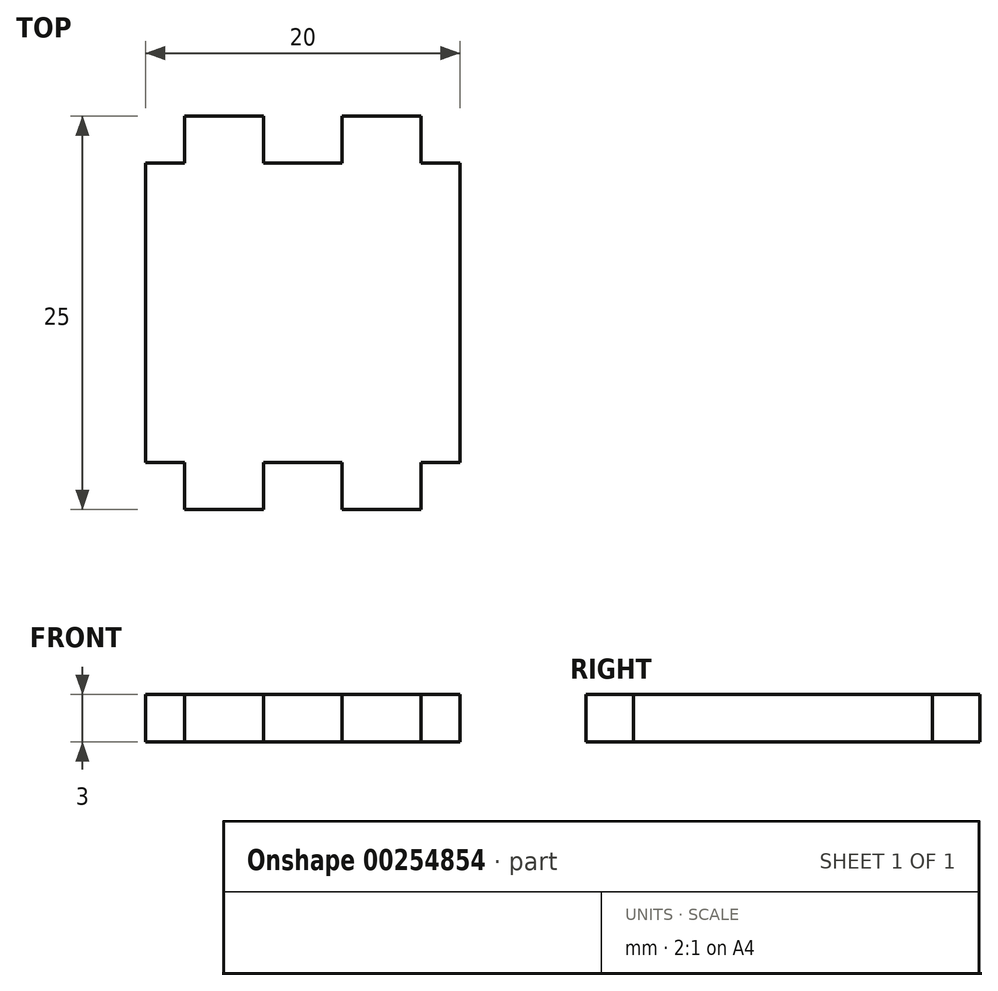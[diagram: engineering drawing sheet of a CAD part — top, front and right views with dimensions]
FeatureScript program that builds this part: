
annotation { "Feature Type Name" : "Feature", "Feature Type Description" : "" }
export const myFeature = defineFeature(function(context is Context, id is Id, definition is map)
    precondition{}
    {
        {
            var Q0;
            Q0=qCreatedBy(makeId("Top.planeOp"),FACE);
            var sketch = newSketch(context, id + "F0", { "sketchPlane" : qUnion([Q0])});
            skLineSegment(sketch, "E0", {"start": v(-10, 0) * mm, "end": v(-10, 9.5) * mm});
            skLineSegment(sketch, "E1", {"start": v(-10, 9.5) * mm, "end": v(-7.5, 9.5) * mm});
            skLineSegment(sketch, "E2", {"start": v(-7.5, 9.5) * mm, "end": v(-7.5, 12.5) * mm});
            skLineSegment(sketch, "E3", {"start": v(-7.5, 12.5) * mm, "end": v(-2.5, 12.5) * mm});
            skLineSegment(sketch, "E4", {"start": v(-2.5, 12.5) * mm, "end": v(-2.5, 9.5) * mm});
            skLineSegment(sketch, "E5", {"start": v(-2.5, 9.5) * mm, "end": v(0, 9.5) * mm});
            skLineSegment(sketch, "E6.MirrorCS", {"start": v(2.5, 9.5) * mm, "end": v(0, 9.5) * mm});
            skLineSegment(sketch, "E7.MirrorCS", {"start": v(2.5, 12.5) * mm, "end": v(2.5, 9.5) * mm});
            skLineSegment(sketch, "E8.MirrorCS", {"start": v(7.5, 12.5) * mm, "end": v(2.5, 12.5) * mm});
            skLineSegment(sketch, "E9.MirrorCS", {"start": v(7.5, 9.5) * mm, "end": v(7.5, 12.5) * mm});
            skLineSegment(sketch, "E10.MirrorCS", {"start": v(10, 9.5) * mm, "end": v(7.5, 9.5) * mm});
            skLineSegment(sketch, "E11.MirrorCS", {"start": v(10, 0) * mm, "end": v(10, 9.5) * mm});
            skLineSegment(sketch, "E12.MirrorCS", {"start": v(10, 0) * mm, "end": v(10, -9.5) * mm});
            skLineSegment(sketch, "E13.MirrorCS", {"start": v(10, -9.5) * mm, "end": v(7.5, -9.5) * mm});
            skLineSegment(sketch, "E14.MirrorCS", {"start": v(7.5, -9.5) * mm, "end": v(7.5, -12.5) * mm});
            skLineSegment(sketch, "E15.MirrorCS", {"start": v(7.5, -12.5) * mm, "end": v(2.5, -12.5) * mm});
            skLineSegment(sketch, "E16.MirrorCS", {"start": v(2.5, -12.5) * mm, "end": v(2.5, -9.5) * mm});
            skLineSegment(sketch, "E17.MirrorCS", {"start": v(2.5, -9.5) * mm, "end": v(0, -9.5) * mm});
            skLineSegment(sketch, "E18.MirrorCS", {"start": v(-2.5, -9.5) * mm, "end": v(0, -9.5) * mm});
            skLineSegment(sketch, "E19.MirrorCS", {"start": v(-2.5, -12.5) * mm, "end": v(-2.5, -9.5) * mm});
            skLineSegment(sketch, "E20.MirrorCS", {"start": v(-7.5, -12.5) * mm, "end": v(-2.5, -12.5) * mm});
            skLineSegment(sketch, "E21.MirrorCS", {"start": v(-7.5, -9.5) * mm, "end": v(-7.5, -12.5) * mm});
            skLineSegment(sketch, "E22.MirrorCS", {"start": v(-10, -9.5) * mm, "end": v(-7.5, -9.5) * mm});
            skLineSegment(sketch, "E23.MirrorCS", {"start": v(-10, 0) * mm, "end": v(-10, -9.5) * mm});
            skSolve(sketch);
        }
        {
            var Q0;
            Q0 = qSketchRegion(id + "F0", true);
            extrude(context, id + "F1", {"entities" : qUnion([Q0]), "depth" : 3 * mm});
        }
    });
